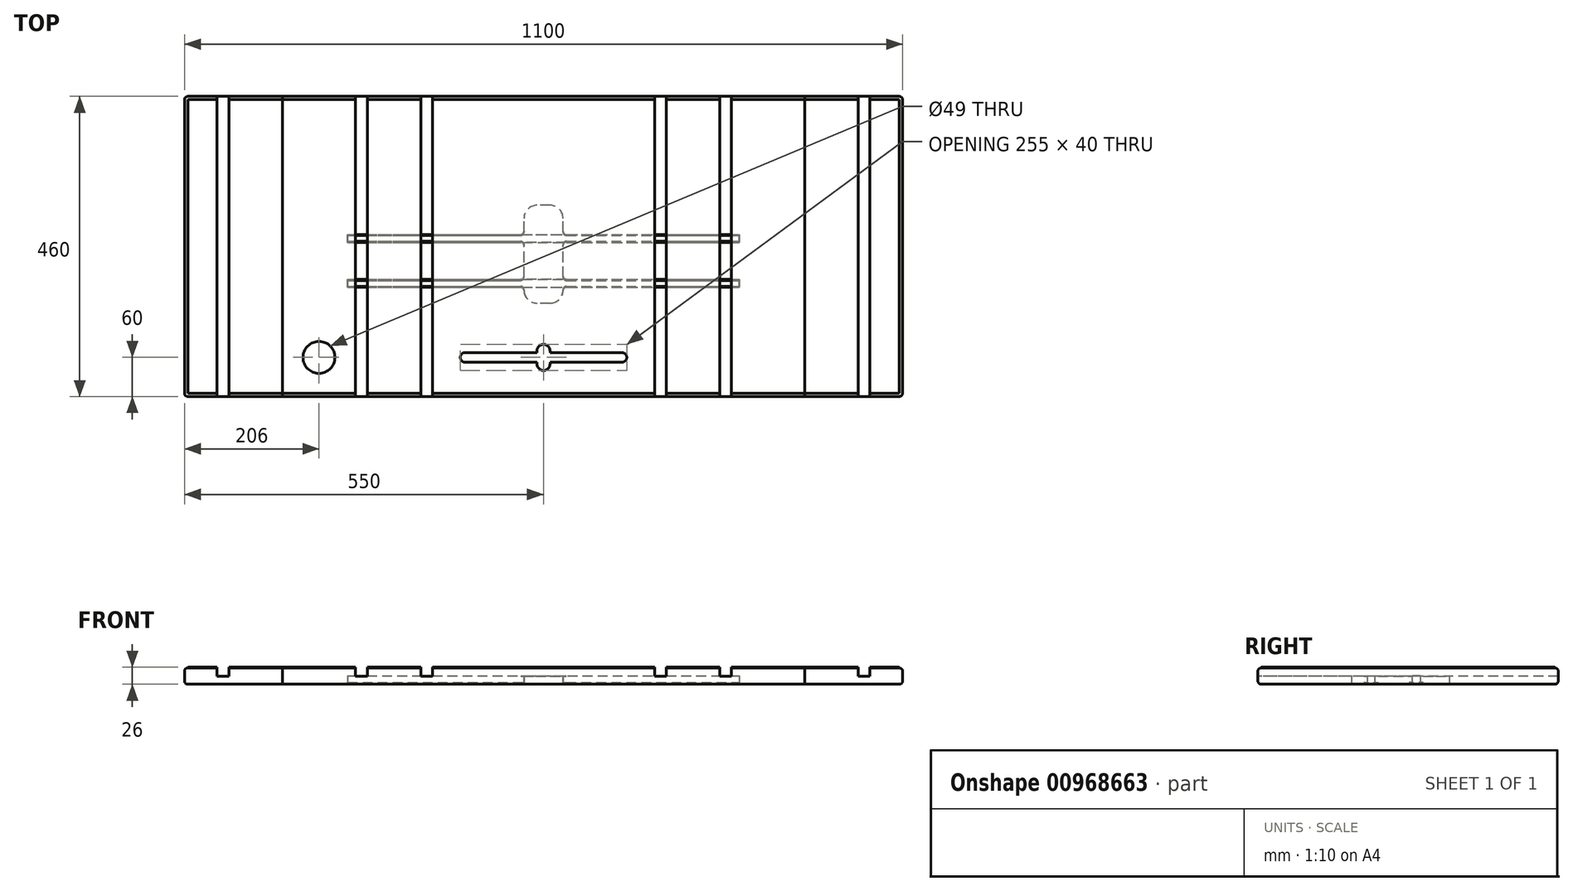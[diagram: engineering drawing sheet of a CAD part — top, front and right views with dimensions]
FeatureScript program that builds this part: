
annotation { "Feature Type Name" : "Feature", "Feature Type Description" : "" }
export const myFeature = defineFeature(function(context is Context, id is Id, definition is map)
    precondition{}
    {
        {
            var Q0;
            Q0=qCreatedBy(makeId("Top.planeOp"),FACE);
            var sketch = newSketch(context, id + "F0", { "sketchPlane" : qUnion([Q0])});
            skLineSegment(sketch, "E0.bottom", {"start": v(-400, 230) * mm, "end": v(400, 230) * mm});
            skLineSegment(sketch, "E0.top", {"start": v(-400, -230) * mm, "end": v(400, -230) * mm});
            skLineSegment(sketch, "E0.left", {"start": v(-400, 230) * mm, "end": v(-400, -230) * mm});
            skLineSegment(sketch, "E0.right", {"start": v(400, 230) * mm, "end": v(400, -230) * mm});
            skPoint(sketch, "E0.middle", {"position": v(0, 0) * mm});
            skSolve(sketch);
        }
        {
            var Q0;
            Q0=makeQuery(id+"F0.imprint","IMPRINT",FACE,{"disambiguationData":[TD([[makeQuery(id+"F0.imprint","IMPRINT",EDGE,{"derivedFrom":sQuery(id+"F0.wireOp",EDGE,"E0.bottom")}),-1.0]])]});
            extrude(context, id + "F1", {"entities" : qUnion([Q0]), "depth" : 25 * mm, "offsetDistance" : 25 * mm});
        }
        {
            var Q0;
            Q0=makeQuery(id+"F1.opExtrude","CAP_EDGE",EDGE,{"disambiguationData":[OSD([sQuery(id+"F0.wireOp",EDGE,"E0.top")])],"isStart":false});
            var Q1;
            Q1=makeQuery(id+"F1.opExtrude","CAP_EDGE",EDGE,{"disambiguationData":[OSD([sQuery(id+"F0.wireOp",EDGE,"E0.bottom")])],"isStart":false});
            var Q2;
            Q2=makeQuery(id+"F1.opExtrude","CAP_EDGE",EDGE,{"disambiguationData":[OSD([sQuery(id+"F0.wireOp",EDGE,"E0.bottom")])],"isStart":true});
            var Q3;
            Q3=makeQuery(id+"F1.opExtrude","CAP_EDGE",EDGE,{"disambiguationData":[OSD([sQuery(id+"F0.wireOp",EDGE,"E0.top")])],"isStart":true});
            fillet(context, id + "F2", {"entities" : qUnion([Q0, Q1, Q2, Q3]), "radius" : 5 * mm, "tangentPropagation" : true, "allowEdgeOverflow" : false});
        }
        {
            var Q0;
            Q0=qCreatedBy(makeId("Front.planeOp"),FACE);
            var sketch = newSketch(context, id + "F3", { "sketchPlane" : qUnion([Q0])});
            skLineSegment(sketch, "E1", {"start": v(0, 0) * mm, "end": v(-170, 0) * mm, "construction": true});
            skLineSegment(sketch, "E2", {"start": v(-170, 0) * mm, "end": v(-270, 0) * mm, "construction": true});
            skLineSegment(sketch, "E3", {"start": v(-170, 0) * mm, "end": v(-170, 25) * mm, "construction": true});
            skLineSegment(sketch, "E4", {"start": v(-270, 0) * mm, "end": v(-270, 25) * mm, "construction": true});
            skLineSegment(sketch, "E5", {"start": v(0, 0) * mm, "end": v(0, 16.31) * mm, "construction": true});
            skLineSegment(sketch, "E6.bottom", {"start": v(-170, 25) * mm, "end": v(-188, 25) * mm});
            skLineSegment(sketch, "E6.top", {"start": v(-170, 12) * mm, "end": v(-188, 12) * mm});
            skLineSegment(sketch, "E6.left", {"start": v(-170, 25) * mm, "end": v(-170, 12) * mm});
            skLineSegment(sketch, "E6.right", {"start": v(-188, 25) * mm, "end": v(-188, 12) * mm});
            skLineSegment(sketch, "E7.bottom", {"start": v(-270, 25) * mm, "end": v(-288, 25) * mm});
            skLineSegment(sketch, "E7.top", {"start": v(-270, 12) * mm, "end": v(-288, 12) * mm});
            skLineSegment(sketch, "E7.left", {"start": v(-270, 25) * mm, "end": v(-270, 12) * mm});
            skLineSegment(sketch, "E7.right", {"start": v(-288, 25) * mm, "end": v(-288, 12) * mm});
            skLineSegment(sketch, "E8.MirrorCS", {"start": v(170, 25) * mm, "end": v(170, 12) * mm});
            skLineSegment(sketch, "E9.MirrorCS", {"start": v(270, 25) * mm, "end": v(270, 12) * mm});
            skLineSegment(sketch, "E10.MirrorCS", {"start": v(170, 0) * mm, "end": v(170, 25) * mm, "construction": true});
            skLineSegment(sketch, "E11.MirrorCS", {"start": v(170, 0) * mm, "end": v(270, 0) * mm, "construction": true});
            skLineSegment(sketch, "E12.MirrorCS", {"start": v(170, 25) * mm, "end": v(188, 25) * mm});
            skLineSegment(sketch, "E13.MirrorCS", {"start": v(170, 12) * mm, "end": v(188, 12) * mm});
            skLineSegment(sketch, "E14.MirrorCS", {"start": v(270, 12) * mm, "end": v(288, 12) * mm});
            skLineSegment(sketch, "E15.MirrorCS", {"start": v(288, 25) * mm, "end": v(288, 12) * mm});
            skLineSegment(sketch, "E16.MirrorCS", {"start": v(188, 25) * mm, "end": v(188, 12) * mm});
            skLineSegment(sketch, "E17.MirrorCS", {"start": v(270, 25) * mm, "end": v(288, 25) * mm});
            skLineSegment(sketch, "E18.MirrorCS", {"start": v(270, 0) * mm, "end": v(270, 25) * mm, "construction": true});
            skSolve(sketch);
        }
        {
            var Q0;
            Q0=qSketchRegion(id+"F3",true);
            extrude(context, id + "F4", {"entities" : qUnion([Q0]), "operationType" : NewBodyOperationType.REMOVE, "endBound" : BoundingType.SYMMETRIC, "oppositeDirection" : true, "depth" : 500 * mm, "offsetDistance" : 25 * mm});
        }
        {
            var Q0;
            Q0=qCreatedBy(makeId("Top.planeOp"),FACE);
            var sketch = newSketch(context, id + "F5", { "sketchPlane" : qUnion([Q0])});
            skLineSegment(sketch, "E19", {"start": v(0, 0) * mm, "end": v(-400, 0) * mm, "construction": true});
            skLineSegment(sketch, "E20", {"start": v(-400, 0) * mm, "end": v(-400, 230) * mm});
            skLineSegment(sketch, "E21", {"start": v(-400, 230) * mm, "end": v(-550, 230) * mm});
            skLineSegment(sketch, "E22", {"start": v(-550, 230) * mm, "end": v(-550, -230) * mm});
            skLineSegment(sketch, "E23", {"start": v(-550, -230) * mm, "end": v(-400, -230) * mm});
            skLineSegment(sketch, "E24", {"start": v(-400, -230) * mm, "end": v(-400, 0) * mm});
            skLineSegment(sketch, "E25", {"start": v(0, 0) * mm, "end": v(0, 33.9) * mm, "construction": true});
            skLineSegment(sketch, "E26.MirrorCS", {"start": v(400, -230) * mm, "end": v(400, 0) * mm});
            skLineSegment(sketch, "E27.MirrorCS", {"start": v(550, 230) * mm, "end": v(550, -230) * mm});
            skLineSegment(sketch, "E28.MirrorCS", {"start": v(400, 0) * mm, "end": v(400, 230) * mm});
            skLineSegment(sketch, "E29.MirrorCS", {"start": v(400, 230) * mm, "end": v(550, 230) * mm});
            skLineSegment(sketch, "E30.MirrorCS", {"start": v(550, -230) * mm, "end": v(400, -230) * mm});
            skSolve(sketch);
        }
        {
            var Q0;
            Q0=makeQuery(id+"F5.imprint","IMPRINT",FACE,{"disambiguationData":[TD([[makeQuery(id+"F5.imprint","IMPRINT",EDGE,{"derivedFrom":sQuery(id+"F5.wireOp",EDGE,"E20")}),1.0]])]});
            var Q1;
            Q1=makeQuery(id+"F5.imprint","IMPRINT",FACE,{"disambiguationData":[TD([[makeQuery(id+"F5.imprint","IMPRINT",EDGE,{"derivedFrom":sQuery(id+"F5.wireOp",EDGE,"E26.MirrorCS")}),-1.0]])]});
            extrude(context, id + "F6", {"entities" : qUnion([Q0, Q1]), "depth" : 25 * mm, "offsetDistance" : 25 * mm});
        }
        {
            var Q0;
            Q0=makeQuery(id+"F6.opExtrude","CAP_EDGE",EDGE,{"disambiguationData":[OSD([sQuery(id+"F5.wireOp",EDGE,"E21")])],"isStart":false});
            var Q1;
            Q1=makeQuery(id+"F6.opExtrude","CAP_EDGE",EDGE,{"disambiguationData":[OSD([sQuery(id+"F5.wireOp",EDGE,"E22")])],"isStart":false});
            var Q2;
            Q2=makeQuery(id+"F6.opExtrude","CAP_EDGE",EDGE,{"disambiguationData":[OSD([sQuery(id+"F5.wireOp",EDGE,"E23")])],"isStart":false});
            var Q3;
            Q3=makeQuery(id+"F6.opExtrude","CAP_EDGE",EDGE,{"disambiguationData":[OSD([sQuery(id+"F5.wireOp",EDGE,"E23")])],"isStart":true});
            var Q4;
            Q4=makeQuery(id+"F6.opExtrude","CAP_EDGE",EDGE,{"disambiguationData":[OSD([sQuery(id+"F5.wireOp",EDGE,"E22")])],"isStart":true});
            var Q5;
            Q5=makeQuery(id+"F6.opExtrude","CAP_EDGE",EDGE,{"disambiguationData":[OSD([sQuery(id+"F5.wireOp",EDGE,"E21")])],"isStart":true});
            var Q6;
            Q6=makeQuery(id+"F6.opExtrude","CAP_EDGE",EDGE,{"disambiguationData":[OSD([sQuery(id+"F5.wireOp",EDGE,"E29.MirrorCS")])],"isStart":true});
            var Q7;
            Q7=makeQuery(id+"F6.opExtrude","CAP_EDGE",EDGE,{"disambiguationData":[OSD([sQuery(id+"F5.wireOp",EDGE,"E27.MirrorCS")])],"isStart":true});
            var Q8;
            Q8=makeQuery(id+"F6.opExtrude","CAP_EDGE",EDGE,{"disambiguationData":[OSD([sQuery(id+"F5.wireOp",EDGE,"E30.MirrorCS")])],"isStart":true});
            var Q9;
            Q9=makeQuery(id+"F6.opExtrude","CAP_EDGE",EDGE,{"disambiguationData":[OSD([sQuery(id+"F5.wireOp",EDGE,"E29.MirrorCS")])],"isStart":false});
            var Q10;
            Q10=makeQuery(id+"F6.opExtrude","CAP_EDGE",EDGE,{"disambiguationData":[OSD([sQuery(id+"F5.wireOp",EDGE,"E30.MirrorCS")])],"isStart":false});
            var Q11;
            Q11=makeQuery(id+"F6.opExtrude","CAP_EDGE",EDGE,{"disambiguationData":[OSD([sQuery(id+"F5.wireOp",EDGE,"E27.MirrorCS")])],"isStart":false});
            var Q12;
            Q12=makeQuery(id+"F6.opExtrude","SWEPT_EDGE",EDGE,{"disambiguationData":[OSD([sQuery(id+"F5.wireOp",EDGE,"E27.MirrorCS"),sQuery(id+"F5.wireOp",EDGE,"E30.MirrorCS")])]});
            var Q13;
            Q13=makeQuery(id+"F6.opExtrude","SWEPT_EDGE",EDGE,{"disambiguationData":[OSD([sQuery(id+"F5.wireOp",EDGE,"E27.MirrorCS"),sQuery(id+"F5.wireOp",EDGE,"E29.MirrorCS")])]});
            var Q14;
            Q14=makeQuery(id+"F6.opExtrude","SWEPT_EDGE",EDGE,{"disambiguationData":[OSD([sQuery(id+"F5.wireOp",EDGE,"E22"),sQuery(id+"F5.wireOp",EDGE,"E23")])]});
            var Q15;
            Q15=makeQuery(id+"F6.opExtrude","SWEPT_EDGE",EDGE,{"disambiguationData":[OSD([sQuery(id+"F5.wireOp",EDGE,"E21"),sQuery(id+"F5.wireOp",EDGE,"E22")])]});
            fillet(context, id + "F7", {"entities" : qUnion([Q0, Q1, Q2, Q3, Q4, Q5, Q6, Q7, Q8, Q9, Q10, Q11, Q12, Q13, Q14, Q15]), "radius" : 5 * mm, "tangentPropagation" : true, "allowEdgeOverflow" : false});
        }
        {
            var Q0;
            Q0=qCreatedBy(makeId("Front.planeOp"),FACE);
            var sketch = newSketch(context, id + "F8", { "sketchPlane" : qUnion([Q0])});
            skLineSegment(sketch, "E31.0.0", {"start": v(-550, 0) * mm, "end": v(-425, 0) * mm, "construction": true});
            skLineSegment(sketch, "E31.0.1", {"start": v(-425, 0) * mm, "end": v(-400, 25) * mm, "construction": true});
            skLineSegment(sketch, "E31.0.2", {"start": v(-400, 25) * mm, "end": v(-550, 25) * mm, "construction": true});
            skLineSegment(sketch, "E31.0.3", {"start": v(-550, 25) * mm, "end": v(-550, 0) * mm, "construction": true});
            skLineSegment(sketch, "E32", {"start": v(-550, 25) * mm, "end": v(-500, 25) * mm, "construction": true});
            skLineSegment(sketch, "E33.bottom", {"start": v(-500, 25) * mm, "end": v(-482, 25) * mm});
            skLineSegment(sketch, "E33.top", {"start": v(-500, 12) * mm, "end": v(-482, 12) * mm});
            skLineSegment(sketch, "E33.left", {"start": v(-500, 25) * mm, "end": v(-500, 12) * mm});
            skLineSegment(sketch, "E33.right", {"start": v(-482, 25) * mm, "end": v(-482, 12) * mm});
            skLineSegment(sketch, "E34", {"start": v(0, 0) * mm, "end": v(0, 12.76) * mm, "construction": true});
            skLineSegment(sketch, "E35.MirrorCS", {"start": v(482, 25) * mm, "end": v(482, 12) * mm});
            skLineSegment(sketch, "E36.MirrorCS", {"start": v(500, 25) * mm, "end": v(500, 12) * mm});
            skLineSegment(sketch, "E37.MirrorCS", {"start": v(500, 25) * mm, "end": v(482, 25) * mm});
            skLineSegment(sketch, "E38.MirrorCS", {"start": v(550, 25) * mm, "end": v(500, 25) * mm, "construction": true});
            skLineSegment(sketch, "E39.MirrorCS", {"start": v(425, 0) * mm, "end": v(400, 25) * mm, "construction": true});
            skLineSegment(sketch, "E40.MirrorCS", {"start": v(500, 12) * mm, "end": v(482, 12) * mm});
            skLineSegment(sketch, "E41.MirrorCS", {"start": v(550, 0) * mm, "end": v(425, 0) * mm, "construction": true});
            skLineSegment(sketch, "E42.MirrorCS", {"start": v(550, 25) * mm, "end": v(550, 0) * mm, "construction": true});
            skLineSegment(sketch, "E43.MirrorCS", {"start": v(400, 25) * mm, "end": v(550, 25) * mm, "construction": true});
            skSolve(sketch);
        }
        {
            var Q0;
            Q0=qSketchRegion(id+"F8",true);
            extrude(context, id + "F9", {"entities" : qUnion([Q0]), "operationType" : NewBodyOperationType.REMOVE, "endBound" : BoundingType.SYMMETRIC, "oppositeDirection" : true, "depth" : 500 * mm, "offsetDistance" : 25 * mm});
        }
        {
            var Q0;
            Q0=qCreatedBy(makeId("Right.planeOp"),FACE);
            var sketch = newSketch(context, id + "F10", { "sketchPlane" : qUnion([Q0])});
            skLineSegment(sketch, "E44.bottom", {"start": v(-86.94, 12) * mm, "end": v(63.06, 12) * mm});
            skLineSegment(sketch, "E44.top", {"start": v(-86.94, -12) * mm, "end": v(63.06, -12) * mm});
            skLineSegment(sketch, "E44.left", {"start": v(-86.94, 12) * mm, "end": v(-86.94, -12) * mm});
            skLineSegment(sketch, "E44.right", {"start": v(63.06, 12) * mm, "end": v(63.06, -12) * mm});
            skPoint(sketch, "E44.middle", {"position": v(-11.94, 0) * mm});
            skSolve(sketch);
        }
        {
            var Q0;
            Q0 = qSketchRegion(id + "F10", true);
            extrude(context, id + "F11", {"entities" : qUnion([Q0]), "operationType" : NewBodyOperationType.REMOVE, "endBound" : BoundingType.SYMMETRIC, "depth" : 60 * mm, "offsetDistance" : 25 * mm});
        }
        {
            var Q0;
            Q0=qCreatedBy(makeId("Right.planeOp"),FACE);
            var sketch = newSketch(context, id + "F12", { "sketchPlane" : qUnion([Q0])});
            skLineSegment(sketch, "E45", {"start": v(-22.09, 0) * mm, "end": v(-52.09, 0) * mm, "construction": true});
            skLineSegment(sketch, "E46", {"start": v(-22.09, 0) * mm, "end": v(-22.09, -12.24) * mm, "construction": true});
            skLineSegment(sketch, "E47", {"start": v(-52.09, 0) * mm, "end": v(-52.09, 3) * mm});
            skLineSegment(sketch, "E48", {"start": v(-52.09, 3) * mm, "end": v(-50.59, 3) * mm});
            skLineSegment(sketch, "E49", {"start": v(-50.59, 3) * mm, "end": v(-50.59, 13) * mm});
            skLineSegment(sketch, "E50", {"start": v(-50.59, 13) * mm, "end": v(-62.59, 13) * mm});
            skLineSegment(sketch, "E51", {"start": v(-62.59, 13) * mm, "end": v(-62.59, 3) * mm});
            skLineSegment(sketch, "E52", {"start": v(-62.59, 3) * mm, "end": v(-61.09, 3) * mm});
            skLineSegment(sketch, "E53", {"start": v(-61.09, 3) * mm, "end": v(-61.09, 0) * mm});
            skLineSegment(sketch, "E54", {"start": v(-61.09, 0) * mm, "end": v(-52.09, 0) * mm});
            skLineSegment(sketch, "E55.MirrorCS", {"start": v(7.91, 3) * mm, "end": v(6.41, 3) * mm});
            skLineSegment(sketch, "E56.MirrorCS", {"start": v(18.41, 3) * mm, "end": v(16.91, 3) * mm});
            skLineSegment(sketch, "E57.MirrorCS", {"start": v(7.91, 0) * mm, "end": v(7.91, 3) * mm});
            skLineSegment(sketch, "E58.MirrorCS", {"start": v(18.41, 13) * mm, "end": v(18.41, 3) * mm});
            skLineSegment(sketch, "E59.MirrorCS", {"start": v(16.91, 0) * mm, "end": v(7.91, 0) * mm});
            skLineSegment(sketch, "E60.MirrorCS", {"start": v(16.91, 3) * mm, "end": v(16.91, 0) * mm});
            skLineSegment(sketch, "E61.MirrorCS", {"start": v(6.41, 13) * mm, "end": v(18.41, 13) * mm});
            skLineSegment(sketch, "E62.MirrorCS", {"start": v(6.41, 3) * mm, "end": v(6.41, 13) * mm});
            skSolve(sketch);
        }
        {
            var Q0;
            Q0 = qSketchRegion(id + "F12", true);
            extrude(context, id + "F13", {"entities" : qUnion([Q0]), "operationType" : NewBodyOperationType.REMOVE, "endBound" : BoundingType.SYMMETRIC, "oppositeDirection" : true, "depth" : 600 * mm, "offsetDistance" : 25 * mm});
        }
        {
            var Q0;
            Q0=makeQuery(id+"F11.boolean.opBoolean","COPY",EDGE,{"derivedFrom":makeQuery(id+"F11.opExtrude","CAP_EDGE",EDGE,{"disambiguationData":[OSD([sQuery(id+"F10.wireOp",EDGE,"E44.left")])],"isStart":false})});
            var Q1;
            Q1=makeQuery(id+"F11.boolean.opBoolean","COPY",EDGE,{"derivedFrom":makeQuery(id+"F11.opExtrude","CAP_EDGE",EDGE,{"disambiguationData":[OSD([sQuery(id+"F10.wireOp",EDGE,"E44.left")])],"isStart":true})});
            var Q2;
            Q2=makeQuery(id+"F11.boolean.opBoolean","COPY",EDGE,{"derivedFrom":makeQuery(id+"F11.opExtrude","CAP_EDGE",EDGE,{"disambiguationData":[OSD([sQuery(id+"F10.wireOp",EDGE,"E44.right")])],"isStart":true})});
            var Q3;
            Q3=makeQuery(id+"F11.boolean.opBoolean","COPY",EDGE,{"derivedFrom":makeQuery(id+"F11.opExtrude","CAP_EDGE",EDGE,{"disambiguationData":[OSD([sQuery(id+"F10.wireOp",EDGE,"E44.right")])],"isStart":false})});
            fillet(context, id + "F14", {"entities" : qUnion([Q0, Q1, Q2, Q3]), "radius" : 20 * mm, "tangentPropagation" : true, "allowEdgeOverflow" : false});
        }
        {
            var Q0;
            Q0=makeQuery(id+"F13.boolean.opBoolean","INTERSECT",EDGE,{"derivedFrom":[makeQuery(id+"F11.boolean.opBoolean","COPY",FACE,{"derivedFrom":makeQuery(id+"F11.opExtrude","CAP_FACE",FACE,{"disambiguationData":[OSD([sQuery(id+"F10.wireOp",EDGE,"E44.bottom"),sQuery(id+"F10.wireOp",EDGE,"E44.top"),sQuery(id+"F10.wireOp",EDGE,"E44.left"),sQuery(id+"F10.wireOp",EDGE,"E44.right")])],"isStart":true})}),makeQuery(id+"F13.opExtrude","SWEPT_FACE",FACE,{"disambiguationData":[OSD([sQuery(id+"F12.wireOp",EDGE,"E51")])]})]});
            var Q1;
            Q1=makeQuery(id+"F13.boolean.opBoolean","INTERSECT",EDGE,{"derivedFrom":[makeQuery(id+"F11.boolean.opBoolean","COPY",FACE,{"derivedFrom":makeQuery(id+"F11.opExtrude","CAP_FACE",FACE,{"disambiguationData":[OSD([sQuery(id+"F10.wireOp",EDGE,"E44.bottom"),sQuery(id+"F10.wireOp",EDGE,"E44.top"),sQuery(id+"F10.wireOp",EDGE,"E44.left"),sQuery(id+"F10.wireOp",EDGE,"E44.right")])],"isStart":true})}),makeQuery(id+"F13.opExtrude","SWEPT_FACE",FACE,{"disambiguationData":[OSD([sQuery(id+"F12.wireOp",EDGE,"E49")])]})]});
            var Q2;
            Q2=makeQuery(id+"F13.boolean.opBoolean","INTERSECT",EDGE,{"derivedFrom":[makeQuery(id+"F11.boolean.opBoolean","COPY",FACE,{"derivedFrom":makeQuery(id+"F11.opExtrude","CAP_FACE",FACE,{"disambiguationData":[OSD([sQuery(id+"F10.wireOp",EDGE,"E44.bottom"),sQuery(id+"F10.wireOp",EDGE,"E44.top"),sQuery(id+"F10.wireOp",EDGE,"E44.left"),sQuery(id+"F10.wireOp",EDGE,"E44.right")])],"isStart":true})}),makeQuery(id+"F13.opExtrude","SWEPT_FACE",FACE,{"disambiguationData":[OSD([sQuery(id+"F12.wireOp",EDGE,"E62.MirrorCS")])]})]});
            var Q3;
            Q3=makeQuery(id+"F13.boolean.opBoolean","INTERSECT",EDGE,{"derivedFrom":[makeQuery(id+"F11.boolean.opBoolean","COPY",FACE,{"derivedFrom":makeQuery(id+"F11.opExtrude","CAP_FACE",FACE,{"disambiguationData":[OSD([sQuery(id+"F10.wireOp",EDGE,"E44.bottom"),sQuery(id+"F10.wireOp",EDGE,"E44.top"),sQuery(id+"F10.wireOp",EDGE,"E44.left"),sQuery(id+"F10.wireOp",EDGE,"E44.right")])],"isStart":true})}),makeQuery(id+"F13.opExtrude","SWEPT_FACE",FACE,{"disambiguationData":[OSD([sQuery(id+"F12.wireOp",EDGE,"E58.MirrorCS")])]})]});
            var Q4;
            Q4=makeQuery(id+"F13.boolean.opBoolean","INTERSECT",EDGE,{"derivedFrom":[makeQuery(id+"F11.boolean.opBoolean","COPY",FACE,{"derivedFrom":makeQuery(id+"F11.opExtrude","CAP_FACE",FACE,{"disambiguationData":[OSD([sQuery(id+"F10.wireOp",EDGE,"E44.bottom"),sQuery(id+"F10.wireOp",EDGE,"E44.top"),sQuery(id+"F10.wireOp",EDGE,"E44.left"),sQuery(id+"F10.wireOp",EDGE,"E44.right")])],"isStart":false})}),makeQuery(id+"F13.opExtrude","SWEPT_FACE",FACE,{"disambiguationData":[OSD([sQuery(id+"F12.wireOp",EDGE,"E51")])]})]});
            var Q5;
            Q5=makeQuery(id+"F13.boolean.opBoolean","INTERSECT",EDGE,{"derivedFrom":[makeQuery(id+"F11.boolean.opBoolean","COPY",FACE,{"derivedFrom":makeQuery(id+"F11.opExtrude","CAP_FACE",FACE,{"disambiguationData":[OSD([sQuery(id+"F10.wireOp",EDGE,"E44.bottom"),sQuery(id+"F10.wireOp",EDGE,"E44.top"),sQuery(id+"F10.wireOp",EDGE,"E44.left"),sQuery(id+"F10.wireOp",EDGE,"E44.right")])],"isStart":false})}),makeQuery(id+"F13.opExtrude","SWEPT_FACE",FACE,{"disambiguationData":[OSD([sQuery(id+"F12.wireOp",EDGE,"E49")])]})]});
            var Q6;
            Q6=makeQuery(id+"F13.boolean.opBoolean","INTERSECT",EDGE,{"derivedFrom":[makeQuery(id+"F11.boolean.opBoolean","COPY",FACE,{"derivedFrom":makeQuery(id+"F11.opExtrude","CAP_FACE",FACE,{"disambiguationData":[OSD([sQuery(id+"F10.wireOp",EDGE,"E44.bottom"),sQuery(id+"F10.wireOp",EDGE,"E44.top"),sQuery(id+"F10.wireOp",EDGE,"E44.left"),sQuery(id+"F10.wireOp",EDGE,"E44.right")])],"isStart":false})}),makeQuery(id+"F13.opExtrude","SWEPT_FACE",FACE,{"disambiguationData":[OSD([sQuery(id+"F12.wireOp",EDGE,"E62.MirrorCS")])]})]});
            var Q7;
            Q7=makeQuery(id+"F13.boolean.opBoolean","INTERSECT",EDGE,{"derivedFrom":[makeQuery(id+"F11.boolean.opBoolean","COPY",FACE,{"derivedFrom":makeQuery(id+"F11.opExtrude","CAP_FACE",FACE,{"disambiguationData":[OSD([sQuery(id+"F10.wireOp",EDGE,"E44.bottom"),sQuery(id+"F10.wireOp",EDGE,"E44.top"),sQuery(id+"F10.wireOp",EDGE,"E44.left"),sQuery(id+"F10.wireOp",EDGE,"E44.right")])],"isStart":false})}),makeQuery(id+"F13.opExtrude","SWEPT_FACE",FACE,{"disambiguationData":[OSD([sQuery(id+"F12.wireOp",EDGE,"E58.MirrorCS")])]})]});
            fillet(context, id + "F15", {"entities" : qUnion([Q0, Q1, Q2, Q3, Q4, Q5, Q6, Q7]), "radius" : 5 * mm, "tangentPropagation" : true, "allowEdgeOverflow" : false});
        }
        {
            var Q0;
            Q0=makeQuery(id+"F13.boolean.opBoolean","INTERSECT",EDGE,{"derivedFrom":[makeQuery(id+"F11.boolean.opBoolean","COPY",FACE,{"derivedFrom":makeQuery(id+"F11.opExtrude","CAP_FACE",FACE,{"disambiguationData":[OSD([sQuery(id+"F10.wireOp",EDGE,"E44.bottom"),sQuery(id+"F10.wireOp",EDGE,"E44.top"),sQuery(id+"F10.wireOp",EDGE,"E44.left"),sQuery(id+"F10.wireOp",EDGE,"E44.right")])],"isStart":true})}),makeQuery(id+"F13.opExtrude","SWEPT_FACE",FACE,{"disambiguationData":[OSD([sQuery(id+"F12.wireOp",EDGE,"E53")])]})]});
            var Q1;
            Q1=makeQuery(id+"F13.boolean.opBoolean","INTERSECT",EDGE,{"derivedFrom":[makeQuery(id+"F11.boolean.opBoolean","COPY",FACE,{"derivedFrom":makeQuery(id+"F11.opExtrude","CAP_FACE",FACE,{"disambiguationData":[OSD([sQuery(id+"F10.wireOp",EDGE,"E44.bottom"),sQuery(id+"F10.wireOp",EDGE,"E44.top"),sQuery(id+"F10.wireOp",EDGE,"E44.left"),sQuery(id+"F10.wireOp",EDGE,"E44.right")])],"isStart":true})}),makeQuery(id+"F13.opExtrude","SWEPT_FACE",FACE,{"disambiguationData":[OSD([sQuery(id+"F12.wireOp",EDGE,"E47")])]})]});
            var Q2;
            Q2=makeQuery(id+"F13.boolean.opBoolean","INTERSECT",EDGE,{"derivedFrom":[makeQuery(id+"F11.boolean.opBoolean","COPY",FACE,{"derivedFrom":makeQuery(id+"F11.opExtrude","CAP_FACE",FACE,{"disambiguationData":[OSD([sQuery(id+"F10.wireOp",EDGE,"E44.bottom"),sQuery(id+"F10.wireOp",EDGE,"E44.top"),sQuery(id+"F10.wireOp",EDGE,"E44.left"),sQuery(id+"F10.wireOp",EDGE,"E44.right")])],"isStart":true})}),makeQuery(id+"F13.opExtrude","SWEPT_FACE",FACE,{"disambiguationData":[OSD([sQuery(id+"F12.wireOp",EDGE,"E57.MirrorCS")])]})]});
            var Q3;
            Q3=makeQuery(id+"F13.boolean.opBoolean","INTERSECT",EDGE,{"derivedFrom":[makeQuery(id+"F11.boolean.opBoolean","COPY",FACE,{"derivedFrom":makeQuery(id+"F11.opExtrude","CAP_FACE",FACE,{"disambiguationData":[OSD([sQuery(id+"F10.wireOp",EDGE,"E44.bottom"),sQuery(id+"F10.wireOp",EDGE,"E44.top"),sQuery(id+"F10.wireOp",EDGE,"E44.left"),sQuery(id+"F10.wireOp",EDGE,"E44.right")])],"isStart":true})}),makeQuery(id+"F13.opExtrude","SWEPT_FACE",FACE,{"disambiguationData":[OSD([sQuery(id+"F12.wireOp",EDGE,"E60.MirrorCS")])]})]});
            var Q4;
            Q4=makeQuery(id+"F13.boolean.opBoolean","INTERSECT",EDGE,{"derivedFrom":[makeQuery(id+"F11.boolean.opBoolean","COPY",FACE,{"derivedFrom":makeQuery(id+"F11.opExtrude","CAP_FACE",FACE,{"disambiguationData":[OSD([sQuery(id+"F10.wireOp",EDGE,"E44.bottom"),sQuery(id+"F10.wireOp",EDGE,"E44.top"),sQuery(id+"F10.wireOp",EDGE,"E44.left"),sQuery(id+"F10.wireOp",EDGE,"E44.right")])],"isStart":false})}),makeQuery(id+"F13.opExtrude","SWEPT_FACE",FACE,{"disambiguationData":[OSD([sQuery(id+"F12.wireOp",EDGE,"E60.MirrorCS")])]})]});
            var Q5;
            Q5=makeQuery(id+"F13.boolean.opBoolean","INTERSECT",EDGE,{"derivedFrom":[makeQuery(id+"F11.boolean.opBoolean","COPY",FACE,{"derivedFrom":makeQuery(id+"F11.opExtrude","CAP_FACE",FACE,{"disambiguationData":[OSD([sQuery(id+"F10.wireOp",EDGE,"E44.bottom"),sQuery(id+"F10.wireOp",EDGE,"E44.top"),sQuery(id+"F10.wireOp",EDGE,"E44.left"),sQuery(id+"F10.wireOp",EDGE,"E44.right")])],"isStart":false})}),makeQuery(id+"F13.opExtrude","SWEPT_FACE",FACE,{"disambiguationData":[OSD([sQuery(id+"F12.wireOp",EDGE,"E57.MirrorCS")])]})]});
            var Q6;
            Q6=makeQuery(id+"F13.boolean.opBoolean","INTERSECT",EDGE,{"derivedFrom":[makeQuery(id+"F11.boolean.opBoolean","COPY",FACE,{"derivedFrom":makeQuery(id+"F11.opExtrude","CAP_FACE",FACE,{"disambiguationData":[OSD([sQuery(id+"F10.wireOp",EDGE,"E44.bottom"),sQuery(id+"F10.wireOp",EDGE,"E44.top"),sQuery(id+"F10.wireOp",EDGE,"E44.left"),sQuery(id+"F10.wireOp",EDGE,"E44.right")])],"isStart":false})}),makeQuery(id+"F13.opExtrude","SWEPT_FACE",FACE,{"disambiguationData":[OSD([sQuery(id+"F12.wireOp",EDGE,"E47")])]})]});
            var Q7;
            Q7=makeQuery(id+"F13.boolean.opBoolean","INTERSECT",EDGE,{"derivedFrom":[makeQuery(id+"F11.boolean.opBoolean","COPY",FACE,{"derivedFrom":makeQuery(id+"F11.opExtrude","CAP_FACE",FACE,{"disambiguationData":[OSD([sQuery(id+"F10.wireOp",EDGE,"E44.bottom"),sQuery(id+"F10.wireOp",EDGE,"E44.top"),sQuery(id+"F10.wireOp",EDGE,"E44.left"),sQuery(id+"F10.wireOp",EDGE,"E44.right")])],"isStart":false})}),makeQuery(id+"F13.opExtrude","SWEPT_FACE",FACE,{"disambiguationData":[OSD([sQuery(id+"F12.wireOp",EDGE,"E53")])]})]});
            fillet(context, id + "F16", {"entities" : qUnion([Q0, Q1, Q2, Q3, Q4, Q5, Q6, Q7]), "radius" : 5 * mm, "tangentPropagation" : true, "allowEdgeOverflow" : false});
        }
        {
            var Q0;
            {var subQ0=sQuery(id+"F5.wireOp",EDGE,"E22");var subQ1=sQuery(id+"F5.wireOp",EDGE,"E21");var subQ2=sQuery(id+"F5.wireOp",EDGE,"E23");Q0=makeQuery(id+"F9.boolean.opBoolean","SPLIT",FACE,{"disambiguationData":[TD([makeQuery(id+"F9.opExtrude","SWEPT_FACE",FACE,{"disambiguationData":[OSD([sQuery(id+"F8.wireOp",EDGE,"E33.left")])]})])],"derivedFrom":makeQuery(id+"F6.opExtrude","CAP_FACE",FACE,{"disambiguationData":[OSD([sQuery(id+"F5.wireOp",EDGE,"E20"),subQ1,subQ0,subQ2,sQuery(id+"F5.wireOp",EDGE,"E24")])],"isStart":false})});}
            var sketch = newSketch(context, id + "F17", { "sketchPlane" : qUnion([Q0])});
            skLineSegment(sketch, "E63.0.0", {"start": v(-400, 225) * mm, "end": v(-482, 225) * mm});
            skLineSegment(sketch, "E63.0.1", {"start": v(-482, 225) * mm, "end": v(-482, -225) * mm});
            skLineSegment(sketch, "E63.0.2", {"start": v(-482, -225) * mm, "end": v(-400, -225) * mm});
            skLineSegment(sketch, "E63.0.3", {"start": v(-400, -225) * mm, "end": v(-400, 225) * mm});
            skLineSegment(sketch, "E64.0.0", {"start": v(-288, -225) * mm, "end": v(-288, 225) * mm});
            skLineSegment(sketch, "E64.0.1", {"start": v(-288, 225) * mm, "end": v(-400, 225) * mm});
            skLineSegment(sketch, "E64.0.2", {"start": v(-400, 225) * mm, "end": v(-400, -225) * mm});
            skLineSegment(sketch, "E64.0.3", {"start": v(-400, -225) * mm, "end": v(-288, -225) * mm});
            skLineSegment(sketch, "E65.0.0", {"start": v(-188, 225) * mm, "end": v(-270, 225) * mm});
            skLineSegment(sketch, "E65.0.1", {"start": v(-270, 225) * mm, "end": v(-270, -225) * mm});
            skLineSegment(sketch, "E65.0.2", {"start": v(-270, -225) * mm, "end": v(-188, -225) * mm});
            skLineSegment(sketch, "E65.0.3", {"start": v(-188, -225) * mm, "end": v(-188, 225) * mm});
            skLineSegment(sketch, "E66.0.0", {"start": v(170, -225) * mm, "end": v(170, 225) * mm});
            skLineSegment(sketch, "E66.0.1", {"start": v(170, 225) * mm, "end": v(-170, 225) * mm});
            skLineSegment(sketch, "E66.0.2", {"start": v(-170, 225) * mm, "end": v(-170, -225) * mm});
            skLineSegment(sketch, "E66.0.3", {"start": v(-170, -225) * mm, "end": v(170, -225) * mm});
            skLineSegment(sketch, "E67.0.0", {"start": v(270, -225) * mm, "end": v(270, 225) * mm});
            skLineSegment(sketch, "E67.0.1", {"start": v(270, 225) * mm, "end": v(188, 225) * mm});
            skLineSegment(sketch, "E67.0.2", {"start": v(188, 225) * mm, "end": v(188, -225) * mm});
            skLineSegment(sketch, "E67.0.3", {"start": v(188, -225) * mm, "end": v(270, -225) * mm});
            skLineSegment(sketch, "E68.0.0", {"start": v(400, 225) * mm, "end": v(288, 225) * mm});
            skLineSegment(sketch, "E68.0.1", {"start": v(288, 225) * mm, "end": v(288, -225) * mm});
            skLineSegment(sketch, "E68.0.2", {"start": v(288, -225) * mm, "end": v(400, -225) * mm});
            skLineSegment(sketch, "E68.0.3", {"start": v(400, -225) * mm, "end": v(400, 225) * mm});
            skLineSegment(sketch, "E69.0.0", {"start": v(482, -225) * mm, "end": v(482, 225) * mm});
            skLineSegment(sketch, "E69.0.1", {"start": v(482, 225) * mm, "end": v(400, 225) * mm});
            skLineSegment(sketch, "E69.0.2", {"start": v(400, 225) * mm, "end": v(400, -225) * mm});
            skLineSegment(sketch, "E69.0.3", {"start": v(400, -225) * mm, "end": v(482, -225) * mm});
            skLineSegment(sketch, "E70.0.0", {"start": v(545, 225) * mm, "end": v(500, 225) * mm});
            skLineSegment(sketch, "E70.0.1", {"start": v(500, 225) * mm, "end": v(500, -225) * mm});
            skLineSegment(sketch, "E70.0.2", {"start": v(500, -225) * mm, "end": v(545, -225) * mm});
            skLineSegment(sketch, "E70.0.3", {"start": v(545, -225) * mm, "end": v(545, 225) * mm});
            skLineSegment(sketch, "E71.bottom", {"start": v(-500, -225) * mm, "end": v(-545, -225) * mm});
            skLineSegment(sketch, "E71.top", {"start": v(-500, 225) * mm, "end": v(-545, 225) * mm});
            skLineSegment(sketch, "E71.left", {"start": v(-500, -225) * mm, "end": v(-500, 225) * mm});
            skLineSegment(sketch, "E71.right", {"start": v(-545, -225) * mm, "end": v(-545, 225) * mm});
            skSolve(sketch);
        }
        {
            var Q0;
            Q0=makeQuery(id+"F17.imprint","IMPRINT",FACE,{"disambiguationData":[TD([[makeQuery(id+"F17.imprint","IMPRINT",EDGE,{"derivedFrom":sQuery(id+"F17.wireOp",EDGE,"E71.bottom")}),1.0]])]});
            var Q1;
            Q1=makeQuery(id+"F17.imprint","IMPRINT",FACE,{"disambiguationData":[TD([[makeQuery(id+"F17.imprint","IMPRINT",EDGE,{"derivedFrom":sQuery(id+"F17.wireOp",EDGE,"E63.0.0")}),1.0]])]});
            var Q2;
            Q2=makeQuery(id+"F17.imprint","IMPRINT",FACE,{"disambiguationData":[TD([[makeQuery(id+"F17.imprint","IMPRINT",EDGE,{"derivedFrom":sQuery(id+"F17.wireOp",EDGE,"E65.0.0")}),1.0]])]});
            var Q3;
            Q3=makeQuery(id+"F17.imprint","IMPRINT",FACE,{"disambiguationData":[TD([[makeQuery(id+"F17.imprint","IMPRINT",EDGE,{"derivedFrom":sQuery(id+"F17.wireOp",EDGE,"E66.0.0")}),1.0]])]});
            var Q4;
            Q4=makeQuery(id+"F17.imprint","IMPRINT",FACE,{"disambiguationData":[TD([[makeQuery(id+"F17.imprint","IMPRINT",EDGE,{"derivedFrom":sQuery(id+"F17.wireOp",EDGE,"E67.0.0")}),1.0]])]});
            var Q5;
            Q5=makeQuery(id+"F17.imprint","IMPRINT",FACE,{"disambiguationData":[TD([[makeQuery(id+"F17.imprint","IMPRINT",EDGE,{"derivedFrom":sQuery(id+"F17.wireOp",EDGE,"E69.0.0")}),1.0]])]});
            var Q6;
            Q6=makeQuery(id+"F17.imprint","IMPRINT",FACE,{"disambiguationData":[TD([[makeQuery(id+"F17.imprint","IMPRINT",EDGE,{"derivedFrom":sQuery(id+"F17.wireOp",EDGE,"E70.0.0")}),1.0]])]});
            extrude(context, id + "F18", {"entities" : qUnion([Q0, Q1, Q2, Q3, Q4, Q5, Q6]), "depth" : 1 * mm, "offsetDistance" : 25 * mm});
        }
        {
            var Q0;
            {var subQ0=sQuery(id+"F0.wireOp",EDGE,"E0.left");var subQ1=sQuery(id+"F0.wireOp",EDGE,"E0.top");var subQ2=sQuery(id+"F0.wireOp",EDGE,"E0.bottom");Q0=makeQuery(id+"F4.boolean.opBoolean","SPLIT",FACE,{"disambiguationData":[TD([makeQuery(id+"F1.opExtrude","SWEPT_FACE",FACE,{"disambiguationData":[OSD([subQ0])]})])],"derivedFrom":makeQuery(id+"F1.opExtrude","CAP_FACE",FACE,{"disambiguationData":[OSD([subQ2,subQ1,subQ0,sQuery(id+"F0.wireOp",EDGE,"E0.right")])],"isStart":false})});}
            var Q1;
            {var subQ0=sQuery(id+"F0.wireOp",EDGE,"E0.right");var subQ1=sQuery(id+"F0.wireOp",EDGE,"E0.bottom");var subQ2=sQuery(id+"F0.wireOp",EDGE,"E0.top");Q1=makeQuery(id+"F4.boolean.opBoolean","SPLIT",FACE,{"disambiguationData":[TD([makeQuery(id+"F1.opExtrude","SWEPT_FACE",FACE,{"disambiguationData":[OSD([subQ0])]})])],"derivedFrom":makeQuery(id+"F1.opExtrude","CAP_FACE",FACE,{"disambiguationData":[OSD([subQ1,subQ2,sQuery(id+"F0.wireOp",EDGE,"E0.left"),subQ0])],"isStart":false})});}
            extrude(context, id + "F19", {"entities" : qUnion([Q0, Q1]), "depth" : 1 * mm, "offsetDistance" : 25 * mm});
        }
        {
            var Q0;
            Q0=makeQuery(id+"F18.opExtrude","CAP_FACE",FACE,{"disambiguationData":[OSD([sQuery(id+"F17.wireOp",EDGE,"E66.0.0"),sQuery(id+"F17.wireOp",EDGE,"E66.0.1"),sQuery(id+"F17.wireOp",EDGE,"E66.0.2"),sQuery(id+"F17.wireOp",EDGE,"E66.0.3")])],"isStart":false});
            var sketch = newSketch(context, id + "F20", { "sketchPlane" : qUnion([Q0])});
            skLineSegment(sketch, "E72", {"start": v(0, 0) * mm, "end": v(0, -225) * mm, "construction": true});
            skLineSegment(sketch, "E73", {"start": v(0, -225) * mm, "end": v(0, -170) * mm, "construction": true});
            skLineSegment(sketch, "E74", {"start": v(0, -170) * mm, "end": v(-120, -170) * mm, "construction": true});
            skLineSegment(sketch, "E75", {"start": v(-120, -170) * mm, "end": v(120, -170) * mm, "construction": true});
            skArc(sketch, "E76.0.startCap", {"start": v(-120, -177.5) * mm, "mid": v(-127.5, -170) * mm, "end": v(-120, -162.5) * mm});
            skArc(sketch, "E76.0.endCap", {"start": v(120, -162.5) * mm, "mid": v(127.5, -170) * mm, "end": v(120, -177.5) * mm});
            skLineSegment(sketch, "E76.0.left", {"start": v(-120, -162.5) * mm, "end": v(120, -162.5) * mm});
            skLineSegment(sketch, "E76.0.right", {"start": v(-120, -177.5) * mm, "end": v(120, -177.5) * mm});
            skLineSegment(sketch, "E77", {"start": v(0, -170) * mm, "end": v(0, -160) * mm, "construction": true});
            skLineSegment(sketch, "E78", {"start": v(0, -160) * mm, "end": v(0, -180) * mm});
            skArc(sketch, "E79.0.startCap", {"start": v(-10, -160) * mm, "mid": v(0, -150) * mm, "end": v(10, -160) * mm});
            skArc(sketch, "E79.0.endCap", {"start": v(10, -180) * mm, "mid": v(0, -190) * mm, "end": v(-10, -180) * mm});
            skLineSegment(sketch, "E79.0.left", {"start": v(10, -160) * mm, "end": v(10, -180) * mm});
            skLineSegment(sketch, "E79.0.right", {"start": v(-10, -160) * mm, "end": v(-10, -180) * mm});
            skSolve(sketch);
        }
        {
            var Q0;
            Q0 = qSketchRegion(id + "F20", true);
            extrude(context, id + "F21", {"entities" : qUnion([Q0]), "operationType" : NewBodyOperationType.REMOVE, "oppositeDirection" : true, "depth" : 1 * mm, "offsetDistance" : 25 * mm});
        }
        {
            var Q0;
            {var subQ0=sQuery(id+"F0.wireOp",EDGE,"E0.left");var subQ1=sQuery(id+"F0.wireOp",EDGE,"E0.top");var subQ2=sQuery(id+"F0.wireOp",EDGE,"E0.bottom");var subQ3=sQuery(id+"F0.wireOp",EDGE,"E0.right");Q0=makeQuery(id+"F19.opExtrude","CAP_FACE",FACE,{"disambiguationData":[OSD([subQ2,subQ1,subQ0,subQ3]),TDD([makeQuery(id+"F4.boolean.opBoolean","SPLIT",FACE,{"disambiguationData":[TD([makeQuery(id+"F1.opExtrude","SWEPT_FACE",FACE,{"disambiguationData":[OSD([subQ0])]})])],"derivedFrom":makeQuery(id+"F1.opExtrude","CAP_FACE",FACE,{"disambiguationData":[OSD([subQ2,subQ1,subQ0,subQ3])],"isStart":false})})])],"isStart":false});}
            var sketch = newSketch(context, id + "F22", { "sketchPlane" : qUnion([Q0])});
            skLineSegment(sketch, "E80", {"start": v(-344, -225) * mm, "end": v(-344, -170) * mm, "construction": true});
            skCircle(sketch, "E81", {"center": v(-344, -170) * mm, "radius": 24.5 * mm});
            skLineSegment(sketch, "E82", {"start": v(-344, -170) * mm, "end": v(-400, -170) * mm, "construction": true});
            skSolve(sketch);
        }
        {
            var Q0;
            Q0 = qSketchRegion(id + "F22", true);
            extrude(context, id + "F23", {"entities" : qUnion([Q0]), "operationType" : NewBodyOperationType.REMOVE, "oppositeDirection" : true, "depth" : 1 * mm, "offsetDistance" : 25 * mm});
        }
    });
